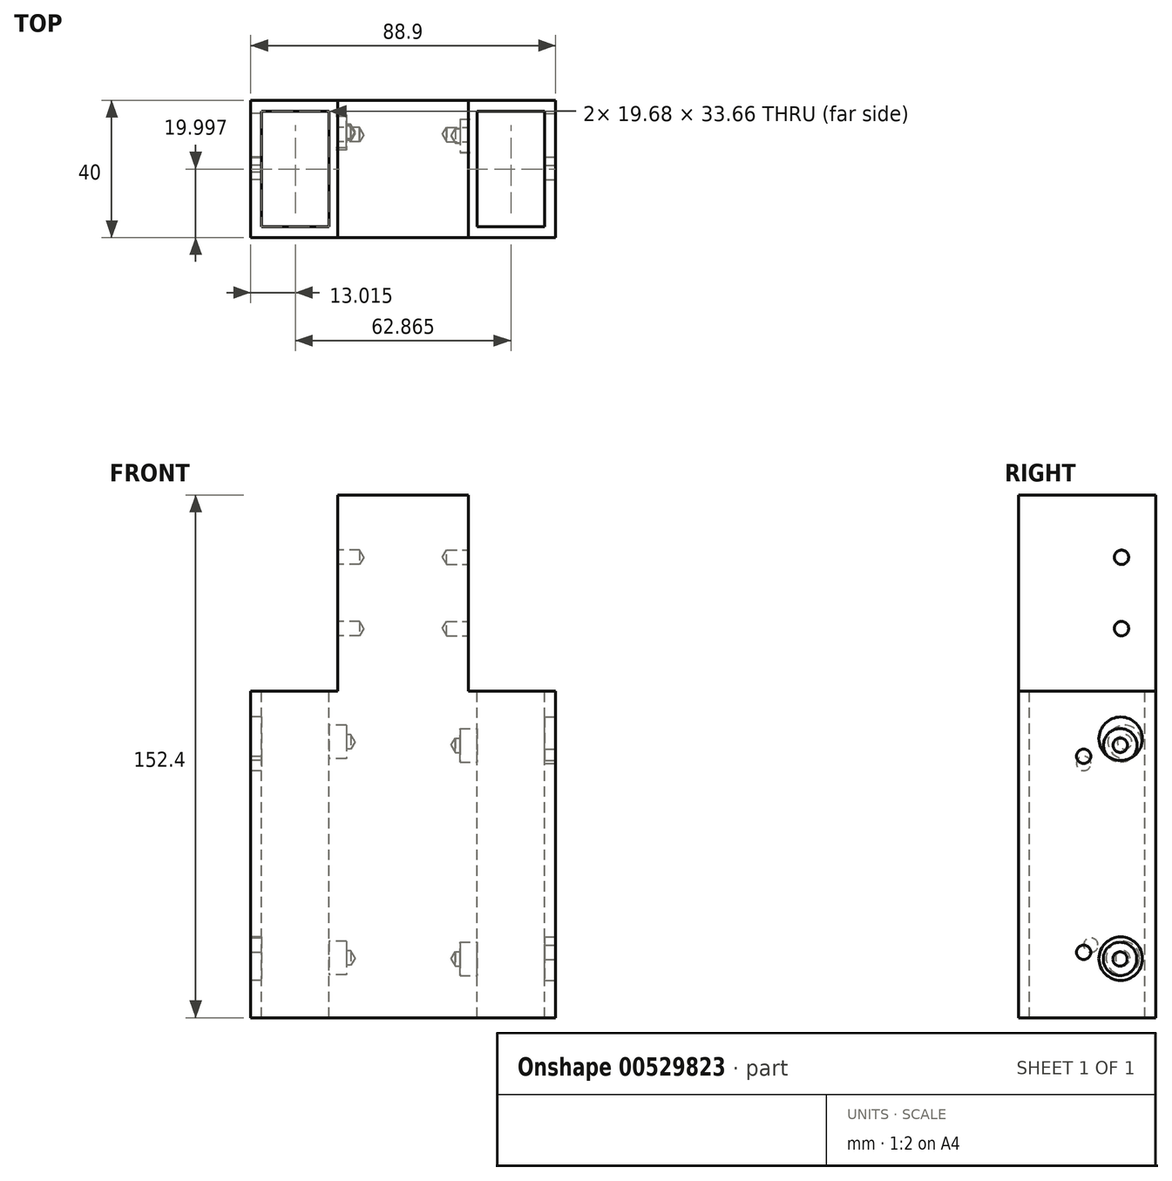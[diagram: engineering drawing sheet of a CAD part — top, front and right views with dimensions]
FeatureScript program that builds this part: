
annotation { "Feature Type Name" : "Feature", "Feature Type Description" : "" }
export const myFeature = defineFeature(function(context is Context, id is Id, definition is map)
    precondition{}
    {
        {
            var Q0;
            Q0=qCreatedBy(makeId("Front.planeOp"),FACE);
            var sketch = newSketch(context, id + "F0", { "sketchPlane" : qUnion([Q0])});
            skLineSegment(sketch, "E0.bottom", {"start": v(-16.67, 98.56) * mm, "end": v(21.43, 98.56) * mm});
            skLineSegment(sketch, "E0.top", {"start": v(-16.67, -53.84) * mm, "end": v(21.43, -53.84) * mm});
            skLineSegment(sketch, "E0.left", {"start": v(-16.67, 98.56) * mm, "end": v(-16.67, -53.84) * mm});
            skLineSegment(sketch, "E0.right", {"start": v(21.43, 98.56) * mm, "end": v(21.43, -53.84) * mm});
            skSolve(sketch);
        }
        {
            var Q0;
            Q0=makeQuery(id+"F0.imprint","IMPRINT",FACE,{"disambiguationData":[TD([[makeQuery(id+"F0.imprint","IMPRINT",EDGE,{"derivedFrom":sQuery(id+"F0.wireOp",EDGE,"E0.bottom")}),-1.0]])]});
            extrude(context, id + "F1", {"entities" : qUnion([Q0]), "depth" : 40 * mm, "offsetDistance" : 25.4 * mm});
        }
        {
            var Q0;
            Q0=makeQuery(id+"F1.opExtrude","SWEPT_FACE",FACE,{"disambiguationData":[OSD([sQuery(id+"F0.wireOp",EDGE,"E0.left")])]});
            var sketch = newSketch(context, id + "F2", { "sketchPlane" : qUnion([Q0])});
            skLineSegment(sketch, "E1.bottom", {"start": v(0, -53.84) * mm, "end": v(40, -53.84) * mm});
            skLineSegment(sketch, "E1.top", {"start": v(0, 41.41) * mm, "end": v(40, 41.41) * mm});
            skLineSegment(sketch, "E1.left", {"start": v(0, -53.84) * mm, "end": v(0, 41.41) * mm});
            skLineSegment(sketch, "E1.right", {"start": v(40, -53.84) * mm, "end": v(40, 41.41) * mm});
            skSolve(sketch);
        }
        {
            var Q0;
            Q0=makeQuery(id+"F1.opExtrude","SWEPT_FACE",FACE,{"disambiguationData":[OSD([sQuery(id+"F0.wireOp",EDGE,"E0.right")])]});
            var sketch = newSketch(context, id + "F3", { "sketchPlane" : qUnion([Q0])});
            skLineSegment(sketch, "E2.bottom", {"start": v(-40, -53.84) * mm, "end": v(0, -53.84) * mm});
            skLineSegment(sketch, "E2.top", {"start": v(-40, 41.41) * mm, "end": v(0, 41.41) * mm});
            skLineSegment(sketch, "E2.left", {"start": v(-40, -53.84) * mm, "end": v(-40, 41.41) * mm});
            skLineSegment(sketch, "E2.right", {"start": v(0, -53.84) * mm, "end": v(0, 41.41) * mm});
            skSolve(sketch);
        }
        {
            var Q0;
            Q0=makeQuery(id+"F3.imprint","IMPRINT",FACE,{"disambiguationData":[TD([[makeQuery(id+"F3.imprint","IMPRINT",EDGE,{"derivedFrom":sQuery(id+"F3.wireOp",EDGE,"E2.bottom")}),1.0]])]});
            extrude(context, id + "F4", {"entities" : qUnion([Q0]), "operationType" : NewBodyOperationType.ADD, "depth" : 25.4 * mm, "offsetDistance" : 25.4 * mm});
        }
        {
            var Q0;
            Q0=makeQuery(id+"F2.imprint","IMPRINT",FACE,{"disambiguationData":[TD([[makeQuery(id+"F2.imprint","IMPRINT",EDGE,{"derivedFrom":sQuery(id+"F2.wireOp",EDGE,"E1.bottom")}),-1.0]])]});
            extrude(context, id + "F5", {"entities" : qUnion([Q0]), "operationType" : NewBodyOperationType.ADD, "depth" : 25.4 * mm, "offsetDistance" : 25.4 * mm});
        }
        {
            var Q0;
            Q0=makeQuery(id+"F5.opExtrude","SWEPT_FACE",FACE,{"disambiguationData":[OSD([sQuery(id+"F2.wireOp",EDGE,"E1.top")])]});
            var sketch = newSketch(context, id + "F6", { "sketchPlane" : qUnion([Q0])});
            skPoint(sketch, "E3", {"position": v(-29.37, -19.05) * mm});
            skPoint(sketch, "E4", {"position": v(33.63, -19.05) * mm});
            skSolve(sketch);
        }
        {
            var Q0;
            {var subQ0=sQuery(id+"F2.wireOp",EDGE,"E1.top");Q0=makeQuery(id+"F6.imprint","IMPRINT",FACE,{"disambiguationData":[TD([[makeQuery(id+"F6.imprint","IMPRINT",EDGE,{"derivedFrom":makeQuery(id+"F5.opExtrude","CAP_EDGE",EDGE,{"disambiguationData":[OSD([subQ0])],"isStart":false})}),1.0]])]});}
            var sketch = newSketch(context, id + "F7", { "sketchPlane" : qUnion([Q0])});
            skLineSegment(sketch, "E5.bottom", {"start": v(-38.9, -3.18) * mm, "end": v(-19.21, -3.18) * mm});
            skLineSegment(sketch, "E5.top", {"start": v(-38.9, -36.83) * mm, "end": v(-19.21, -36.83) * mm});
            skLineSegment(sketch, "E5.left", {"start": v(-38.9, -3.18) * mm, "end": v(-38.9, -36.83) * mm});
            skLineSegment(sketch, "E5.right", {"start": v(-19.21, -3.18) * mm, "end": v(-19.21, -36.83) * mm});
            skSolve(sketch);
        }
        {
            var Q0;
            Q0 = qSketchRegion(id + "F7", true);
            extrude(context, id + "F8", {"entities" : qUnion([Q0]), "operationType" : NewBodyOperationType.REMOVE, "endBound" : BoundingType.UP_TO_NEXT, "oppositeDirection" : true, "depth" : 127 * mm, "offsetDistance" : 25.4 * mm});
        }
        {
            var Q0;
            Q0=makeQuery(id+"F4.opExtrude","SWEPT_FACE",FACE,{"disambiguationData":[OSD([sQuery(id+"F3.wireOp",EDGE,"E2.top")])]});
            var sketch = newSketch(context, id + "F9", { "sketchPlane" : qUnion([Q0])});
            skLineSegment(sketch, "E6.bottom", {"start": v(23.97, -36.83) * mm, "end": v(43.65, -36.83) * mm});
            skLineSegment(sketch, "E6.top", {"start": v(23.97, -3.18) * mm, "end": v(43.65, -3.17) * mm});
            skLineSegment(sketch, "E6.left", {"start": v(23.97, -36.83) * mm, "end": v(23.97, -3.18) * mm});
            skLineSegment(sketch, "E6.right", {"start": v(43.65, -36.83) * mm, "end": v(43.65, -3.18) * mm});
            skSolve(sketch);
        }
        {
            var Q0;
            Q0=makeQuery(id+"F9.imprint","IMPRINT",FACE,{"disambiguationData":[TD([[makeQuery(id+"F9.imprint","IMPRINT",EDGE,{"derivedFrom":sQuery(id+"F9.wireOp",EDGE,"E6.bottom")}),1.0]])]});
            extrude(context, id + "F10", {"entities" : qUnion([Q0]), "operationType" : NewBodyOperationType.REMOVE, "endBound" : BoundingType.UP_TO_NEXT, "oppositeDirection" : true, "depth" : 25.4 * mm, "offsetDistance" : 25.4 * mm});
        }
        {
            var Q0;
            Q0=makeQuery(id+"F1.opExtrude","SWEPT_FACE",FACE,{"disambiguationData":[OSD([sQuery(id+"F0.wireOp",EDGE,"E0.left")])]});
            var sketch = newSketch(context, id + "F11", { "sketchPlane" : qUnion([Q0])});
            skCircle(sketch, "E7", {"center": v(10, 80.38) * mm, "radius": 3.18 * mm});
            skCircle(sketch, "E8", {"center": v(10, 59.6) * mm, "radius": 3.18 * mm});
            skSolve(sketch);
        }
        {
            var Q0;
            Q0=sQuery(id+"F11.wireOp",VERTEX,"E7.center");
            var Q1;
            Q1=sQuery(id+"F11.wireOp",VERTEX,"E8.center");
            var Q2;
            Q2=makeQuery(id+"F1.opExtrude","SWEPT_BODY",BODY,{"disambiguationData":[OSD([sQuery(id+"F0.wireOp",EDGE,"E0.bottom"),sQuery(id+"F0.wireOp",EDGE,"E0.top"),sQuery(id+"F0.wireOp",EDGE,"E0.left"),sQuery(id+"F0.wireOp",EDGE,"E0.right")])]});
            hole(context, id + "F12", {"style" : HoleStyle.SIMPLE, "endStyle" : HoleEndStyle.BLIND, "standardTappedOrClearance" : lookupTablePath({ "standard" : "ISO", "engagement" : "75%", "pitch" : "0.8 mm", "size" : "M5", "type" : "Tapped" }), "standardBlindInLast" : lookupTablePath({ "standard" : "ISO", "engagement" : "75%", "pitch" : "0.8 mm", "size" : "M5", "type" : "Tapped" }), "holeDiameter" : 4.2 * mm, "showTappedDepth" : true, "holeDepth" : 6.35 * mm, "isTappedThrough" : true, "tappedDepth" : 3.95 * mm, "tapClearance" : 3, "locations" : qUnion([Q0, Q1]), "scope" : qUnion([Q2]), "majorDiameter" : 5 * mm});
        }
        {
            var Q0;
            Q0=makeQuery(id+"F1.opExtrude","SWEPT_FACE",FACE,{"disambiguationData":[OSD([sQuery(id+"F0.wireOp",EDGE,"E0.right")])]});
            var sketch = newSketch(context, id + "F13", { "sketchPlane" : qUnion([Q0])});
            skCircle(sketch, "E9", {"center": v(-9.93, 80.38) * mm, "radius": 3.18 * mm});
            skCircle(sketch, "E10", {"center": v(-9.93, 59.6) * mm, "radius": 3.18 * mm});
            skSolve(sketch);
        }
        {
            var Q0;
            Q0=sQuery(id+"F13.wireOp",VERTEX,"E9.center");
            var Q1;
            Q1=sQuery(id+"F13.wireOp",VERTEX,"E10.center");
            var Q2;
            Q2=makeQuery(id+"F1.opExtrude","SWEPT_BODY",BODY,{"disambiguationData":[OSD([sQuery(id+"F0.wireOp",EDGE,"E0.bottom"),sQuery(id+"F0.wireOp",EDGE,"E0.top"),sQuery(id+"F0.wireOp",EDGE,"E0.left"),sQuery(id+"F0.wireOp",EDGE,"E0.right")])]});
            hole(context, id + "F14", {"style" : HoleStyle.SIMPLE, "endStyle" : HoleEndStyle.BLIND, "standardTappedOrClearance" : lookupTablePath({ "standard" : "ISO", "engagement" : "75%", "pitch" : "0.8 mm", "size" : "M5", "type" : "Tapped" }), "standardBlindInLast" : lookupTablePath({ "standard" : "ISO", "engagement" : "75%", "pitch" : "0.8 mm", "size" : "M5", "type" : "Tapped" }), "holeDiameter" : 4.2 * mm, "showTappedDepth" : true, "holeDepth" : 6.35 * mm, "isTappedThrough" : true, "tappedDepth" : 3.95 * mm, "tapClearance" : 3, "locations" : qUnion([Q0, Q1]), "scope" : qUnion([Q2]), "majorDiameter" : 5 * mm});
        }
        {
            var Q0;
            Q0=makeQuery(id+"F5.opExtrude","CAP_FACE",FACE,{"disambiguationData":[OSD([sQuery(id+"F2.wireOp",EDGE,"E1.bottom"),sQuery(id+"F2.wireOp",EDGE,"E1.top"),sQuery(id+"F2.wireOp",EDGE,"E1.left"),sQuery(id+"F2.wireOp",EDGE,"E1.right")])],"isStart":false});
            var sketch = newSketch(context, id + "F15", { "sketchPlane" : qUnion([Q0])});
            skCircle(sketch, "E11", {"center": v(10.16, 27.46) * mm, "radius": 6.35 * mm});
            skSolve(sketch);
        }
        {
            var Q0;
            Q0=makeQuery(id+"F15.imprint","IMPRINT",FACE,{"disambiguationData":[TD([[makeQuery(id+"F15.imprint","IMPRINT",EDGE,{"derivedFrom":sQuery(id+"F15.wireOp",EDGE,"E11")}),1.0]])]});
            extrude(context, id + "F16", {"entities" : qUnion([Q0]), "operationType" : NewBodyOperationType.REMOVE, "oppositeDirection" : true, "depth" : 5.08 * mm, "offsetDistance" : 25.4 * mm});
        }
        {
            var Q0;
            Q0=makeQuery(id+"F8.boolean.opBoolean","COPY",FACE,{"derivedFrom":makeQuery(id+"F8.opExtrude","SWEPT_FACE",FACE,{"disambiguationData":[OSD([sQuery(id+"F7.wireOp",EDGE,"E5.right")])]})});
            var sketch = newSketch(context, id + "F17", { "sketchPlane" : qUnion([Q0])});
            skCircle(sketch, "E12", {"center": v(9.02, 26.57) * mm, "radius": 0.72 * mm});
            skSolve(sketch);
        }
        {
            var Q0;
            Q0=sQuery(id+"F17.wireOp",VERTEX,"E12.center");
            var Q1;
            Q1=makeQuery(id+"F1.opExtrude","SWEPT_BODY",BODY,{"disambiguationData":[OSD([sQuery(id+"F0.wireOp",EDGE,"E0.bottom"),sQuery(id+"F0.wireOp",EDGE,"E0.top"),sQuery(id+"F0.wireOp",EDGE,"E0.left"),sQuery(id+"F0.wireOp",EDGE,"E0.right")])]});
            hole(context, id + "F18", {"style" : HoleStyle.C_BORE, "endStyle" : HoleEndStyle.BLIND, "standardTappedOrClearance" : lookupTablePath({ "standard" : "ISO", "engagement" : "75%", "pitch" : "0.8 mm", "size" : "M5", "type" : "Tapped" }), "standardBlindInLast" : lookupTablePath({ "standard" : "ISO", "engagement" : "75%", "pitch" : "0.8 mm", "size" : "M5", "type" : "Tapped" }), "holeDiameter" : 4.2 * mm, "cBoreDiameter" : 9.75 * mm, "cBoreDepth" : 5 * mm, "showTappedDepth" : true, "holeDepth" : 6.35 * mm, "isTappedThrough" : true, "tappedDepth" : 3.95 * mm, "tapClearance" : 3, "locations" : qUnion([Q0]), "scope" : qUnion([Q1]), "majorDiameter" : 5 * mm});
        }
        {
            var Q0;
            Q0=makeQuery(id+"F5.opExtrude","CAP_FACE",FACE,{"disambiguationData":[OSD([sQuery(id+"F2.wireOp",EDGE,"E1.bottom"),sQuery(id+"F2.wireOp",EDGE,"E1.top"),sQuery(id+"F2.wireOp",EDGE,"E1.left"),sQuery(id+"F2.wireOp",EDGE,"E1.right")])],"isStart":false});
            var sketch = newSketch(context, id + "F19", { "sketchPlane" : qUnion([Q0])});
            skCircle(sketch, "E13", {"center": v(20.96, 20.27) * mm, "radius": 2.1 * mm});
            skSolve(sketch);
        }
        {
            var Q0;
            Q0=makeQuery(id+"F19.imprint","IMPRINT",FACE,{"disambiguationData":[TD([[makeQuery(id+"F19.imprint","IMPRINT",EDGE,{"derivedFrom":sQuery(id+"F19.wireOp",EDGE,"E13")}),1.0]])]});
            extrude(context, id + "F20", {"entities" : qUnion([Q0]), "operationType" : NewBodyOperationType.REMOVE, "endBound" : BoundingType.UP_TO_NEXT, "oppositeDirection" : true, "depth" : 25.4 * mm, "offsetDistance" : 25.4 * mm});
        }
        {
            var Q0;
            Q0=makeQuery(id+"F5.opExtrude","CAP_FACE",FACE,{"disambiguationData":[OSD([sQuery(id+"F2.wireOp",EDGE,"E1.bottom"),sQuery(id+"F2.wireOp",EDGE,"E1.top"),sQuery(id+"F2.wireOp",EDGE,"E1.left"),sQuery(id+"F2.wireOp",EDGE,"E1.right")])],"isStart":false});
            var sketch = newSketch(context, id + "F21", { "sketchPlane" : qUnion([Q0])});
            skCircle(sketch, "E14", {"center": v(10.16, -36.6) * mm, "radius": 6.35 * mm});
            skSolve(sketch);
        }
        {
            var Q0;
            Q0=makeQuery(id+"F21.imprint","IMPRINT",FACE,{"disambiguationData":[TD([[makeQuery(id+"F21.imprint","IMPRINT",EDGE,{"derivedFrom":sQuery(id+"F21.wireOp",EDGE,"E14")}),1.0]])]});
            extrude(context, id + "F22", {"entities" : qUnion([Q0]), "operationType" : NewBodyOperationType.REMOVE, "oppositeDirection" : true, "depth" : 5.08 * mm, "offsetDistance" : 25.4 * mm});
        }
        {
            var Q0;
            Q0=makeQuery(id+"F8.boolean.opBoolean","COPY",FACE,{"derivedFrom":makeQuery(id+"F8.opExtrude","SWEPT_FACE",FACE,{"disambiguationData":[OSD([sQuery(id+"F7.wireOp",EDGE,"E5.right")])]})});
            var sketch = newSketch(context, id + "F23", { "sketchPlane" : qUnion([Q0])});
            skCircle(sketch, "E15", {"center": v(9.56, -36.44) * mm, "radius": 0.94 * mm});
            skSolve(sketch);
        }
        {
            var Q0;
            Q0=sQuery(id+"F23.wireOp",VERTEX,"E15.center");
            var Q1;
            Q1=makeQuery(id+"F1.opExtrude","SWEPT_BODY",BODY,{"disambiguationData":[OSD([sQuery(id+"F0.wireOp",EDGE,"E0.bottom"),sQuery(id+"F0.wireOp",EDGE,"E0.top"),sQuery(id+"F0.wireOp",EDGE,"E0.left"),sQuery(id+"F0.wireOp",EDGE,"E0.right")])]});
            hole(context, id + "F24", {"style" : HoleStyle.C_BORE, "endStyle" : HoleEndStyle.BLIND, "standardTappedOrClearance" : lookupTablePath({ "standard" : "ISO", "engagement" : "75%", "pitch" : "0.8 mm", "size" : "M5", "type" : "Tapped" }), "standardBlindInLast" : lookupTablePath({ "standard" : "ISO", "engagement" : "75%", "pitch" : "0.8 mm", "size" : "M5", "type" : "Tapped" }), "holeDiameter" : 4.2 * mm, "cBoreDiameter" : 9.75 * mm, "cBoreDepth" : 5 * mm, "showTappedDepth" : true, "holeDepth" : 6.35 * mm, "isTappedThrough" : true, "tappedDepth" : 3.95 * mm, "tapClearance" : 3, "locations" : qUnion([Q0]), "scope" : qUnion([Q1]), "majorDiameter" : 5 * mm});
        }
        {
            var Q0;
            Q0=makeQuery(id+"F5.opExtrude","CAP_FACE",FACE,{"disambiguationData":[OSD([sQuery(id+"F2.wireOp",EDGE,"E1.bottom"),sQuery(id+"F2.wireOp",EDGE,"E1.top"),sQuery(id+"F2.wireOp",EDGE,"E1.left"),sQuery(id+"F2.wireOp",EDGE,"E1.right")])],"isStart":false});
            var sketch = newSketch(context, id + "F25", { "sketchPlane" : qUnion([Q0])});
            skCircle(sketch, "E16", {"center": v(18.86, -32.7) * mm, "radius": 2.1 * mm});
            skSolve(sketch);
        }
        {
            var Q0;
            Q0=makeQuery(id+"F25.imprint","IMPRINT",FACE,{"disambiguationData":[TD([[makeQuery(id+"F25.imprint","IMPRINT",EDGE,{"derivedFrom":sQuery(id+"F25.wireOp",EDGE,"E16")}),1.0]])]});
            extrude(context, id + "F26", {"entities" : qUnion([Q0]), "operationType" : NewBodyOperationType.REMOVE, "endBound" : BoundingType.UP_TO_NEXT, "oppositeDirection" : true, "depth" : 25.4 * mm, "offsetDistance" : 25.4 * mm});
        }
        {
            var Q0;
            Q0=makeQuery(id+"F4.opExtrude","CAP_FACE",FACE,{"disambiguationData":[OSD([sQuery(id+"F3.wireOp",EDGE,"E2.bottom"),sQuery(id+"F3.wireOp",EDGE,"E2.top"),sQuery(id+"F3.wireOp",EDGE,"E2.left"),sQuery(id+"F3.wireOp",EDGE,"E2.right")])],"isStart":false});
            var sketch = newSketch(context, id + "F27", { "sketchPlane" : qUnion([Q0])});
            skCircle(sketch, "E17", {"center": v(-10.16, 27.47) * mm, "radius": 6.35 * mm});
            skSolve(sketch);
        }
        {
            var Q0;
            Q0=makeQuery(id+"F27.imprint","IMPRINT",FACE,{"disambiguationData":[TD([[makeQuery(id+"F27.imprint","IMPRINT",EDGE,{"derivedFrom":sQuery(id+"F27.wireOp",EDGE,"E17")}),1.0]])]});
            extrude(context, id + "F28", {"entities" : qUnion([Q0]), "operationType" : NewBodyOperationType.REMOVE, "endBound" : BoundingType.UP_TO_NEXT, "oppositeDirection" : true, "depth" : 25.4 * mm, "offsetDistance" : 25.4 * mm});
        }
        {
            var Q0;
            Q0=makeQuery(id+"F4.opExtrude","CAP_FACE",FACE,{"disambiguationData":[OSD([sQuery(id+"F3.wireOp",EDGE,"E2.bottom"),sQuery(id+"F3.wireOp",EDGE,"E2.top"),sQuery(id+"F3.wireOp",EDGE,"E2.left"),sQuery(id+"F3.wireOp",EDGE,"E2.right")])],"isStart":false});
            var sketch = newSketch(context, id + "F29", { "sketchPlane" : qUnion([Q0])});
            skCircle(sketch, "E18", {"center": v(-20.96, 22.36) * mm, "radius": 2.1 * mm});
            skSolve(sketch);
        }
        {
            var Q0;
            Q0=makeQuery(id+"F29.imprint","IMPRINT",FACE,{"disambiguationData":[TD([[makeQuery(id+"F29.imprint","IMPRINT",EDGE,{"derivedFrom":sQuery(id+"F29.wireOp",EDGE,"E18")}),1.0]])]});
            extrude(context, id + "F30", {"entities" : qUnion([Q0]), "operationType" : NewBodyOperationType.REMOVE, "endBound" : BoundingType.UP_TO_NEXT, "oppositeDirection" : true, "depth" : 25.4 * mm, "offsetDistance" : 25.4 * mm});
        }
        {
            var Q0;
            Q0=makeQuery(id+"F4.opExtrude","CAP_FACE",FACE,{"disambiguationData":[OSD([sQuery(id+"F3.wireOp",EDGE,"E2.bottom"),sQuery(id+"F3.wireOp",EDGE,"E2.top"),sQuery(id+"F3.wireOp",EDGE,"E2.left"),sQuery(id+"F3.wireOp",EDGE,"E2.right")])],"isStart":false});
            var sketch = newSketch(context, id + "F31", { "sketchPlane" : qUnion([Q0])});
            skCircle(sketch, "E19", {"center": v(-10.16, -36.62) * mm, "radius": 6.35 * mm});
            skCircle(sketch, "E20", {"center": v(-20.96, -34.79) * mm, "radius": 2.1 * mm});
            skSolve(sketch);
        }
        {
            var Q0;
            Q0=makeQuery(id+"F31.imprint","IMPRINT",FACE,{"disambiguationData":[TD([[makeQuery(id+"F31.imprint","IMPRINT",EDGE,{"derivedFrom":sQuery(id+"F31.wireOp",EDGE,"E19")}),1.0]])]});
            var Q1;
            Q1=makeQuery(id+"F31.imprint","IMPRINT",FACE,{"disambiguationData":[TD([[makeQuery(id+"F31.imprint","IMPRINT",EDGE,{"derivedFrom":sQuery(id+"F31.wireOp",EDGE,"E20")}),1.0]])]});
            extrude(context, id + "F32", {"entities" : qUnion([Q0, Q1]), "operationType" : NewBodyOperationType.REMOVE, "endBound" : BoundingType.UP_TO_NEXT, "oppositeDirection" : true, "depth" : 25.4 * mm, "offsetDistance" : 25.4 * mm});
        }
        {
            var Q0;
            Q0=makeQuery(id+"F10.boolean.opBoolean","COPY",FACE,{"derivedFrom":makeQuery(id+"F10.opExtrude","SWEPT_FACE",FACE,{"disambiguationData":[OSD([sQuery(id+"F9.wireOp",EDGE,"E6.left")])]})});
            var sketch = newSketch(context, id + "F33", { "sketchPlane" : qUnion([Q0])});
            skCircle(sketch, "E21", {"center": v(-10.27, 25.59) * mm, "radius": 1.28 * mm});
            skSolve(sketch);
        }
        {
            var Q0;
            Q0=sQuery(id+"F33.wireOp",VERTEX,"E21.center");
            var Q1;
            Q1=makeQuery(id+"F1.opExtrude","SWEPT_BODY",BODY,{"disambiguationData":[OSD([sQuery(id+"F0.wireOp",EDGE,"E0.bottom"),sQuery(id+"F0.wireOp",EDGE,"E0.top"),sQuery(id+"F0.wireOp",EDGE,"E0.left"),sQuery(id+"F0.wireOp",EDGE,"E0.right")])]});
            hole(context, id + "F34", {"style" : HoleStyle.C_BORE, "endStyle" : HoleEndStyle.BLIND, "standardTappedOrClearance" : lookupTablePath({ "standard" : "ISO", "engagement" : "75%", "pitch" : "0.8 mm", "size" : "M5", "type" : "Tapped" }), "standardBlindInLast" : lookupTablePath({ "standard" : "ISO", "engagement" : "75%", "pitch" : "0.8 mm", "size" : "M5", "type" : "Tapped" }), "holeDiameter" : 4.2 * mm, "cBoreDiameter" : 9.75 * mm, "cBoreDepth" : 5 * mm, "showTappedDepth" : true, "holeDepth" : 6.35 * mm, "isTappedThrough" : true, "tappedDepth" : 3.95 * mm, "tapClearance" : 3, "locations" : qUnion([Q0]), "scope" : qUnion([Q1]), "majorDiameter" : 5 * mm});
        }
        {
            var Q0;
            Q0=makeQuery(id+"F10.boolean.opBoolean","COPY",FACE,{"derivedFrom":makeQuery(id+"F10.opExtrude","SWEPT_FACE",FACE,{"disambiguationData":[OSD([sQuery(id+"F9.wireOp",EDGE,"E6.left")])]})});
            var sketch = newSketch(context, id + "F35", { "sketchPlane" : qUnion([Q0])});
            skCircle(sketch, "E22", {"center": v(-10.35, -36.72) * mm, "radius": 0.78 * mm});
            skSolve(sketch);
        }
        {
            var Q0;
            Q0=sQuery(id+"F35.wireOp",VERTEX,"E22.center");
            var Q1;
            Q1=makeQuery(id+"F1.opExtrude","SWEPT_BODY",BODY,{"disambiguationData":[OSD([sQuery(id+"F0.wireOp",EDGE,"E0.bottom"),sQuery(id+"F0.wireOp",EDGE,"E0.top"),sQuery(id+"F0.wireOp",EDGE,"E0.left"),sQuery(id+"F0.wireOp",EDGE,"E0.right")])]});
            hole(context, id + "F36", {"style" : HoleStyle.C_BORE, "endStyle" : HoleEndStyle.BLIND, "standardTappedOrClearance" : lookupTablePath({ "standard" : "ISO", "engagement" : "75%", "pitch" : "0.8 mm", "size" : "M5", "type" : "Tapped" }), "standardBlindInLast" : lookupTablePath({ "standard" : "ISO", "engagement" : "75%", "pitch" : "0.8 mm", "size" : "M5", "type" : "Tapped" }), "holeDiameter" : 4.2 * mm, "cBoreDiameter" : 9.75 * mm, "cBoreDepth" : 5 * mm, "showTappedDepth" : true, "holeDepth" : 6.35 * mm, "isTappedThrough" : true, "tappedDepth" : 3.95 * mm, "tapClearance" : 3, "locations" : qUnion([Q0]), "scope" : qUnion([Q1]), "majorDiameter" : 5 * mm});
        }
    });
